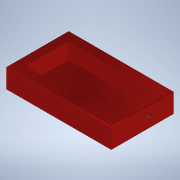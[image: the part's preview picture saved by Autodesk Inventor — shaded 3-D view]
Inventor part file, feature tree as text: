
AUTODESK INVENTOR PART (.ipt)
format: ipt  version: 2022 (Build 260153000, 153)  size: 184,320 bytes
history: native  units: mm
features: sketch x5, hole x3, extrude x2, fillet x1, chamfer x1
ambient origin geometry x8: Origin, YZ Plane, XZ Plane, XY Plane, X Axis, Y Axis, Z Axis, Center Point
bodies: Volumenkörper1 (feature_tree)
feature tree (12):
  extrude  "Extrusion1"  Depth=139.7mm
  extrude  "Extrusion2"  Depth=192.0mm
  fillet  "Rundung1"  Radius=96.0mm
  chamfer  "Fase1"  Distance=36.0mm
  sketch  "Skizze4"  dims[d10=4.0mm d11=2.0mm d12=2.0mm d13=45.0deg]
  hole  "Bohrung7"  [1 undecoded]
  sketch  "Sketch12"  dims[d153=24.0mm d154=24.0mm]
  hole  "Hole10"  [1 undecoded]
  hole  "Hole11"  [1 undecoded]
  sketch  "Skizze1"  dims[d0=234.95mm d2=139.7mm]
  sketch  "Skizze2"  dims[d3=44.45mm d4=0.0mm d5=192.0mm d7=96.0mm d8=36.0mm d9=0.0mm]
  sketch  "Sketch13"  dims[d155=5.0mm d156=5.0mm d157=24.0mm d158=5.0mm d159=5.0mm d160=24.0mm d161=24.0mm d162=5.0mm d163=5.0mm d164=24.0mm d165=5.0mm d166=24.0mm d167=5.0mm d168=24.0mm d169=3.242mm d170=6.0mm d171=8.0mm d172=4.6mm d173=14.3117mm d174=20.0mm d175=20.594885mm d206=55.0mm d207=23.0mm d208=7.95mm d209=6.924mm d210=0.624793mm d211=8.304mm d212=12.878mm d213=2.0mm d214=14.3117mm d215=11.628mm d216=20.594885mm d217=25.0mm d218=25.0mm d219=30.0mm d221=25.0mm d222=30.0mm d224=25.0mm d227=5.105mm d228=6.0mm d229=9.779mm d230=2.0mm d231=14.3117mm d232=8.0mm d233=20.594885mm]
note: 3 required parameter values undecoded (feature->parameter linkage not recoverable at this tier; creation-order binding heuristic only, values carry confidence <= 0.55)
